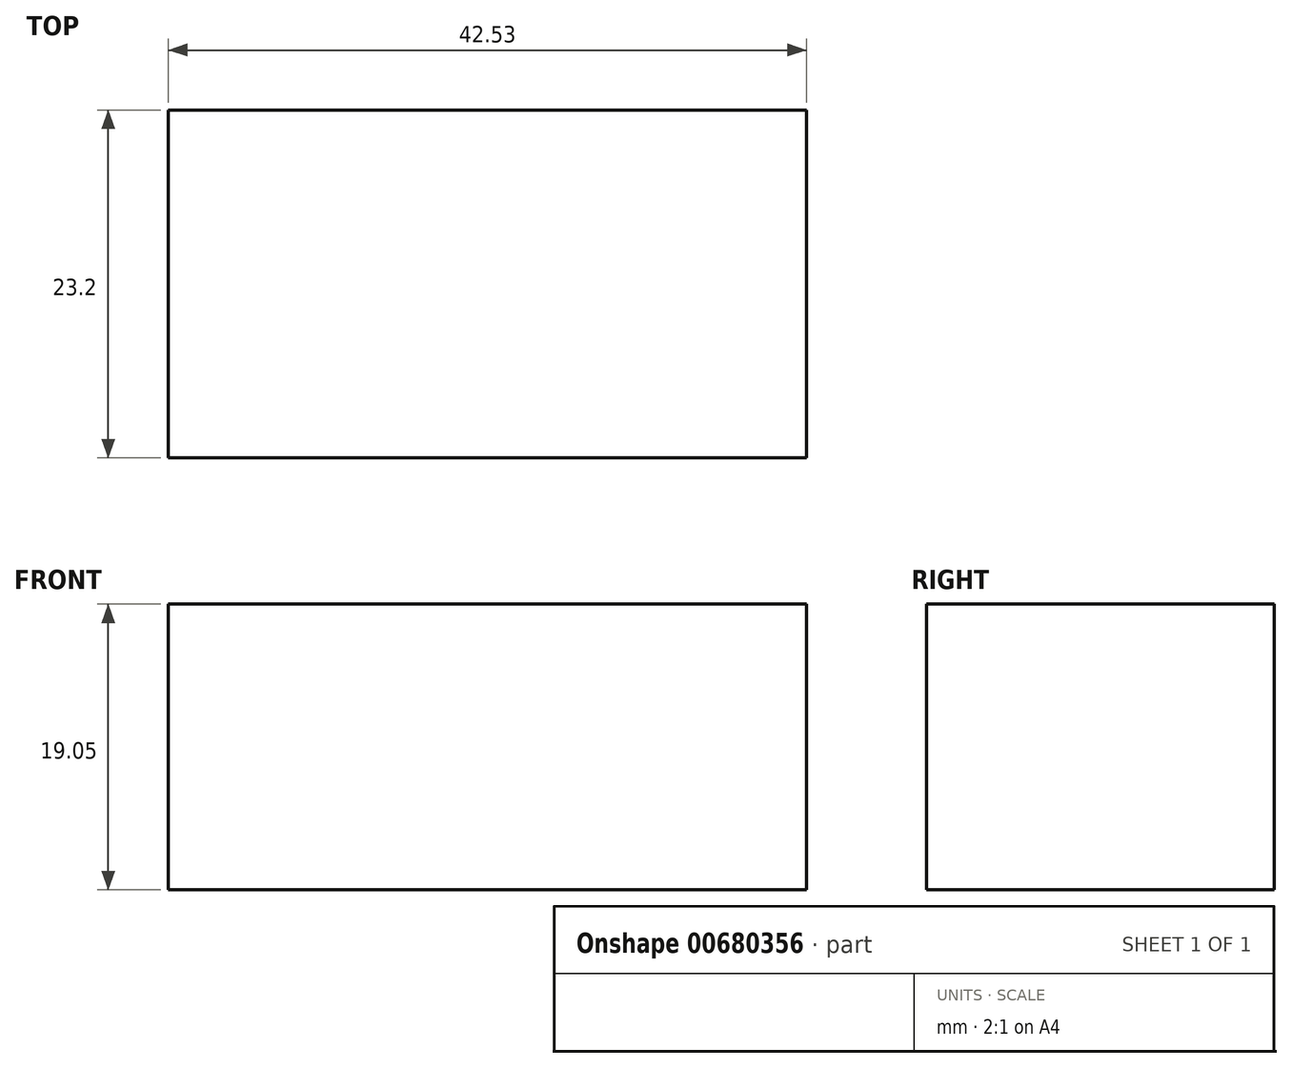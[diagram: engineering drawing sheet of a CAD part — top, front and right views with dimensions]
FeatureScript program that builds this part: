
annotation { "Feature Type Name" : "Feature", "Feature Type Description" : "" }
export const myFeature = defineFeature(function(context is Context, id is Id, definition is map)
    precondition{}
    {
        {
            var Q0;
            Q0=qCreatedBy(makeId("Top.planeOp"),FACE);
            var sketch = newSketch(context, id + "F0", { "sketchPlane" : qUnion([Q0])});
            skLineSegment(sketch, "E0.bottom", {"start": v(16.9, 11.6) * mm, "end": v(-25.63, 11.6) * mm});
            skLineSegment(sketch, "E0.top", {"start": v(16.9, -11.6) * mm, "end": v(-25.63, -11.6) * mm});
            skLineSegment(sketch, "E0.left", {"start": v(16.9, 11.6) * mm, "end": v(16.9, -11.6) * mm});
            skLineSegment(sketch, "E0.right", {"start": v(-25.63, 11.6) * mm, "end": v(-25.63, -11.6) * mm});
            skPoint(sketch, "E0.middle", {"position": v(-4.37, 0) * mm});
            skSolve(sketch);
        }
        {
            var Q0;
            Q0=makeQuery(id+"F0.imprint","IMPRINT",FACE,{"disambiguationData":[TD([[makeQuery(id+"F0.imprint","IMPRINT",EDGE,{"derivedFrom":sQuery(id+"F0.wireOp",EDGE,"E0.bottom")}),1.0]])]});
            extrude(context, id + "F1", {"entities" : qUnion([Q0]), "depth" : 19.05 * mm, "offsetDistance" : 25.4 * mm});
        }
    });
